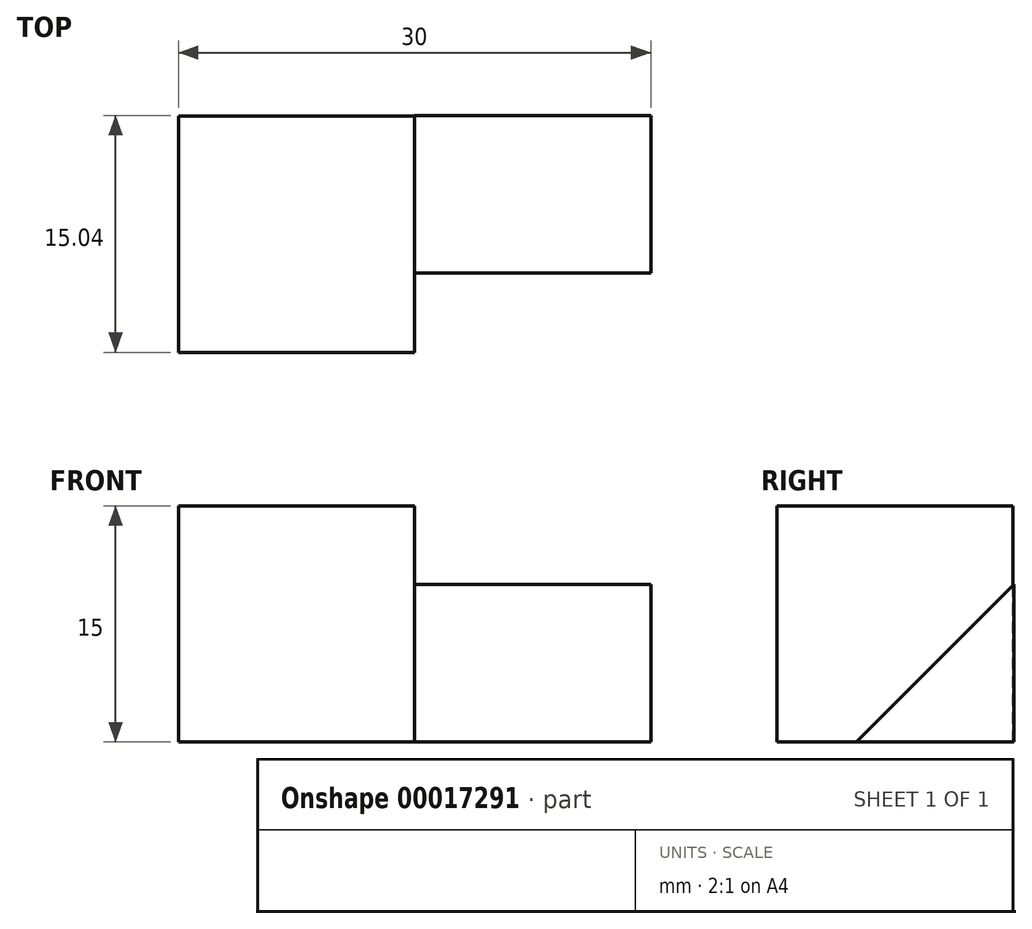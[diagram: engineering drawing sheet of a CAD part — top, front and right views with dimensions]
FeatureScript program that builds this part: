
annotation { "Feature Type Name" : "Feature", "Feature Type Description" : "" }
export const myFeature = defineFeature(function(context is Context, id is Id, definition is map)
    precondition{}
    {
        {
            var Q0;
            Q0=qCreatedBy(makeId("Front.planeOp"),FACE);
            var sketch = newSketch(context, id + "F0", { "sketchPlane" : qUnion([Q0])});
            skLineSegment(sketch, "E0.bottom", {"start": v(0, 0) * mm, "end": v(-15, 0) * mm});
            skLineSegment(sketch, "E0.top", {"start": v(0, 15) * mm, "end": v(-15, 15) * mm});
            skLineSegment(sketch, "E0.left", {"start": v(0, 0) * mm, "end": v(0, 15) * mm});
            skLineSegment(sketch, "E0.right", {"start": v(-15, 0) * mm, "end": v(-15, 15) * mm});
            skSolve(sketch);
        }
        {
            var Q0;
            Q0 = qSketchRegion(id + "F0", true);
            extrude(context, id + "F1", {"entities" : qUnion([Q0]), "oppositeDirection" : true, "depth" : 15 * mm});
        }
        {
            var Q0;
            Q0=qCreatedBy(makeId("Right.planeOp"),FACE);
            var sketch = newSketch(context, id + "F2", { "sketchPlane" : qUnion([Q0])});
            skLineSegment(sketch, "E1", {"start": v(15.04, 0) * mm, "end": v(15.04, 10) * mm});
            skLineSegment(sketch, "E2", {"start": v(15.04, 10) * mm, "end": v(5.04, 0) * mm});
            skLineSegment(sketch, "E3", {"start": v(5.04, 0) * mm, "end": v(15.04, 0) * mm});
            skSolve(sketch);
        }
        {
            var Q0;
            Q0=makeQuery(id+"F2.imprint","IMPRINT",FACE,{"disambiguationData":[TD([[makeQuery(id+"F2.imprint","IMPRINT",EDGE,{"derivedFrom":sQuery(id+"F2.wireOp",EDGE,"E1")}),1.0]])]});
            extrude(context, id + "F3", {"entities" : qUnion([Q0]), "operationType" : NewBodyOperationType.ADD, "depth" : 15 * mm});
        }
    });
